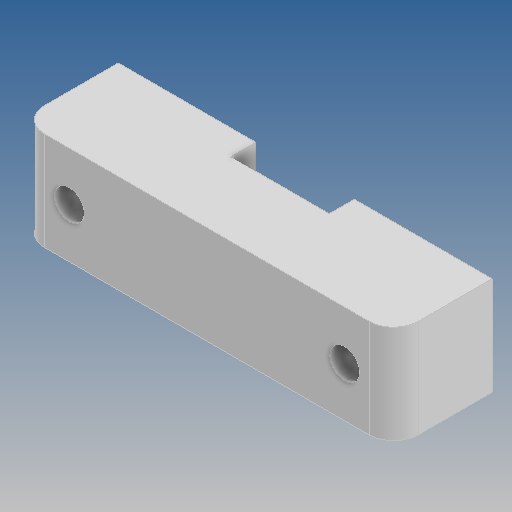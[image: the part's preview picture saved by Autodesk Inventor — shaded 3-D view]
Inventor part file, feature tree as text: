
AUTODESK INVENTOR PART (.ipt)
format: ipt  version: 2020 (Build 240168000, 168)  size: 130,048 bytes
history: native  units: mm
features: sketch x3, extrude x2, other x2, hole x1, fillet x1, reference x1
ambient origin geometry x8: Origin, YZ Plane, XZ Plane, XY Plane, X Axis, Y Axis, Z Axis, Center Point
bodies: Solid1 (feature_tree)
feature tree (10):
  extrude  "Extrusion1"  Depth=20.0mm
  extrude  "Extrusion5"  Depth=20.0mm
  hole  "Hole1"  [1 undecoded]
  fillet  "Fillet3"  Radius=20.0mm
  sketch  "Sketch1"  dims[d0=76.0mm d1=20.0mm]
  sketch  "Sketch6"  dims[d2=20.0mm d3=0.0mm d16=0.3mm]
  reference  "Reference10"
  sketch  "Sketch7"  dims[d17=0.3mm d18=0.3mm d19=20.0mm d20=0.0mm d21=10.0mm d22=10.0mm d23=6.0mm d24=6.0mm d25=4.0mm d26=2.0mm d27=90.0deg d28=8.0mm d29=20.594885mm d30=5.0mm]
  other  "30-00 Injectomat suplimentar.iam"
  other  "0008-30-1009 Adaptor Ac:1"
note: 1 required parameter value undecoded (feature->parameter linkage not recoverable at this tier; creation-order binding heuristic only, values carry confidence <= 0.55)
